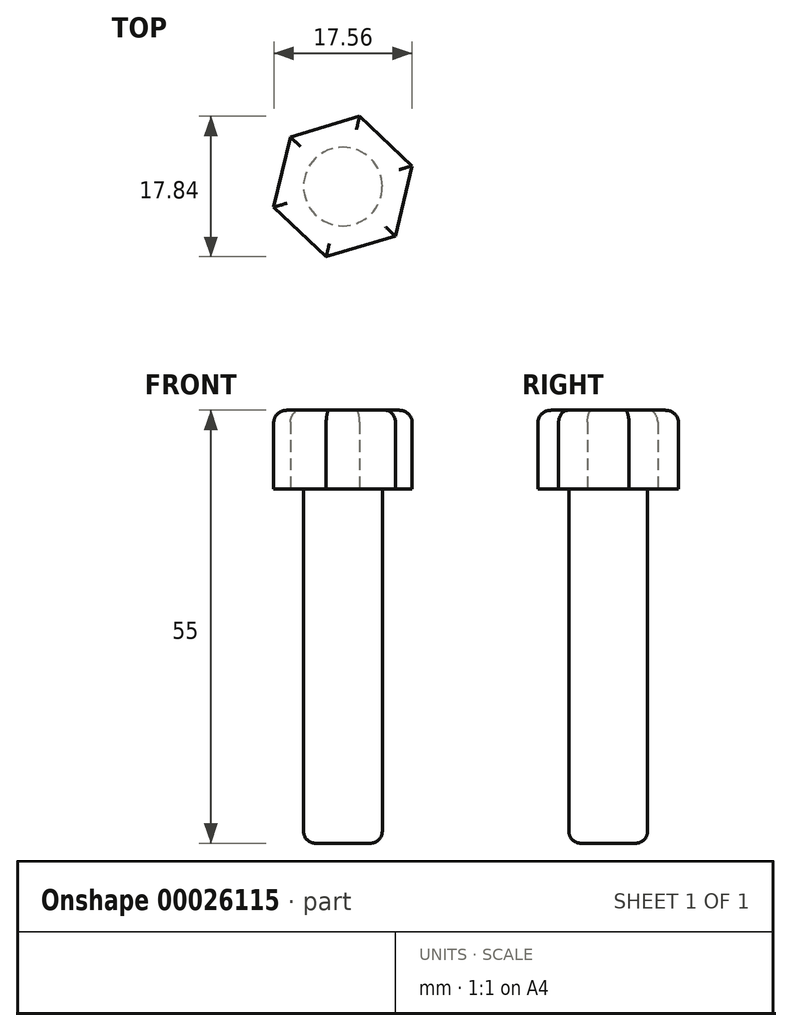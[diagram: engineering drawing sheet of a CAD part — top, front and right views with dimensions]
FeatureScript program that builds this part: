
annotation { "Feature Type Name" : "Feature", "Feature Type Description" : "" }
export const myFeature = defineFeature(function(context is Context, id is Id, definition is map)
    precondition{}
    {
        {
            var Q0;
            Q0=qCreatedBy(makeId("Top.planeOp"),FACE);
            var sketch = newSketch(context, id + "F0", { "sketchPlane" : qUnion([Q0])});
            skCircle(sketch, "E0.cCircle", {"center": v(0, 0) * mm, "radius": 7.94 * mm, "construction": true});
            skLineSegment(sketch, "E0.0", {"start": v(2.12, 8.92) * mm, "end": v(8.78, 2.62) * mm});
            skLineSegment(sketch, "E0.1", {"start": v(8.78, 2.62) * mm, "end": v(6.66, -6.3) * mm});
            skLineSegment(sketch, "E0.2", {"start": v(6.66, -6.3) * mm, "end": v(-2.12, -8.92) * mm});
            skLineSegment(sketch, "E0.3", {"start": v(-2.12, -8.92) * mm, "end": v(-8.78, -2.62) * mm});
            skLineSegment(sketch, "E0.4", {"start": v(-8.78, -2.62) * mm, "end": v(-6.66, 6.3) * mm});
            skLineSegment(sketch, "E0.5", {"start": v(-6.66, 6.3) * mm, "end": v(2.12, 8.92) * mm});
            skPoint(sketch, "E0.0.midPoint", {"position": v(5.45, 5.77) * mm});
            skSolve(sketch);
        }
        {
            var Q0;
            Q0=makeQuery(id+"F0.imprint","IMPRINT",FACE,{"disambiguationData":[TD([[makeQuery(id+"F0.imprint","IMPRINT",EDGE,{"derivedFrom":sQuery(id+"F0.wireOp",EDGE,"E0.0")}),-1.0]])]});
            extrude(context, id + "F1", {"entities" : qUnion([Q0]), "depth" : 10 * mm});
        }
        {
            var Q0;
            Q0=makeQuery(id+"F1.opExtrude","CAP_FACE",FACE,{"disambiguationData":[OSD([sQuery(id+"F0.wireOp",EDGE,"E0.0"),sQuery(id+"F0.wireOp",EDGE,"E0.1"),sQuery(id+"F0.wireOp",EDGE,"E0.2"),sQuery(id+"F0.wireOp",EDGE,"E0.3"),sQuery(id+"F0.wireOp",EDGE,"E0.4"),sQuery(id+"F0.wireOp",EDGE,"E0.5")])],"isStart":true});
            var sketch = newSketch(context, id + "F2", { "sketchPlane" : qUnion([Q0])});
            skCircle(sketch, "E1", {"center": v(0, 0) * mm, "radius": 5 * mm});
            skSolve(sketch);
        }
        {
            var Q0;
            Q0 = qSketchRegion(id + "F2", true);
            extrude(context, id + "F3", {"entities" : qUnion([Q0]), "operationType" : NewBodyOperationType.ADD, "depth" : 45 * mm});
        }
        {
            var Q0;
            Q0=makeQuery(id+"F1.opExtrude","CAP_EDGE",EDGE,{"disambiguationData":[OSD([sQuery(id+"F0.wireOp",EDGE,"E0.1")])],"isStart":false});
            var Q1;
            Q1=makeQuery(id+"F1.opExtrude","CAP_EDGE",EDGE,{"disambiguationData":[OSD([sQuery(id+"F0.wireOp",EDGE,"E0.0")])],"isStart":false});
            var Q2;
            Q2=makeQuery(id+"F1.opExtrude","CAP_EDGE",EDGE,{"disambiguationData":[OSD([sQuery(id+"F0.wireOp",EDGE,"E0.5")])],"isStart":false});
            var Q3;
            Q3=makeQuery(id+"F1.opExtrude","CAP_EDGE",EDGE,{"disambiguationData":[OSD([sQuery(id+"F0.wireOp",EDGE,"E0.4")])],"isStart":false});
            var Q4;
            Q4=makeQuery(id+"F1.opExtrude","CAP_EDGE",EDGE,{"disambiguationData":[OSD([sQuery(id+"F0.wireOp",EDGE,"E0.3")])],"isStart":false});
            var Q5;
            Q5=makeQuery(id+"F1.opExtrude","CAP_EDGE",EDGE,{"disambiguationData":[OSD([sQuery(id+"F0.wireOp",EDGE,"E0.2")])],"isStart":false});
            fillet(context, id + "F4", {"entities" : qUnion([Q0, Q1, Q2, Q3, Q4, Q5]), "radius" : 1.5 * mm, "tangentPropagation" : true, "allowEdgeOverflow" : false});
        }
        {
            var Q0;
            Q0=makeQuery(id+"F3.opExtrude","CAP_EDGE",EDGE,{"disambiguationData":[OSD([sQuery(id+"F2.wireOp",EDGE,"E1")])],"isStart":false});
            fillet(context, id + "F5", {"entities" : qUnion([Q0]), "radius" : 1.5 * mm, "tangentPropagation" : true, "allowEdgeOverflow" : false});
        }
    });
